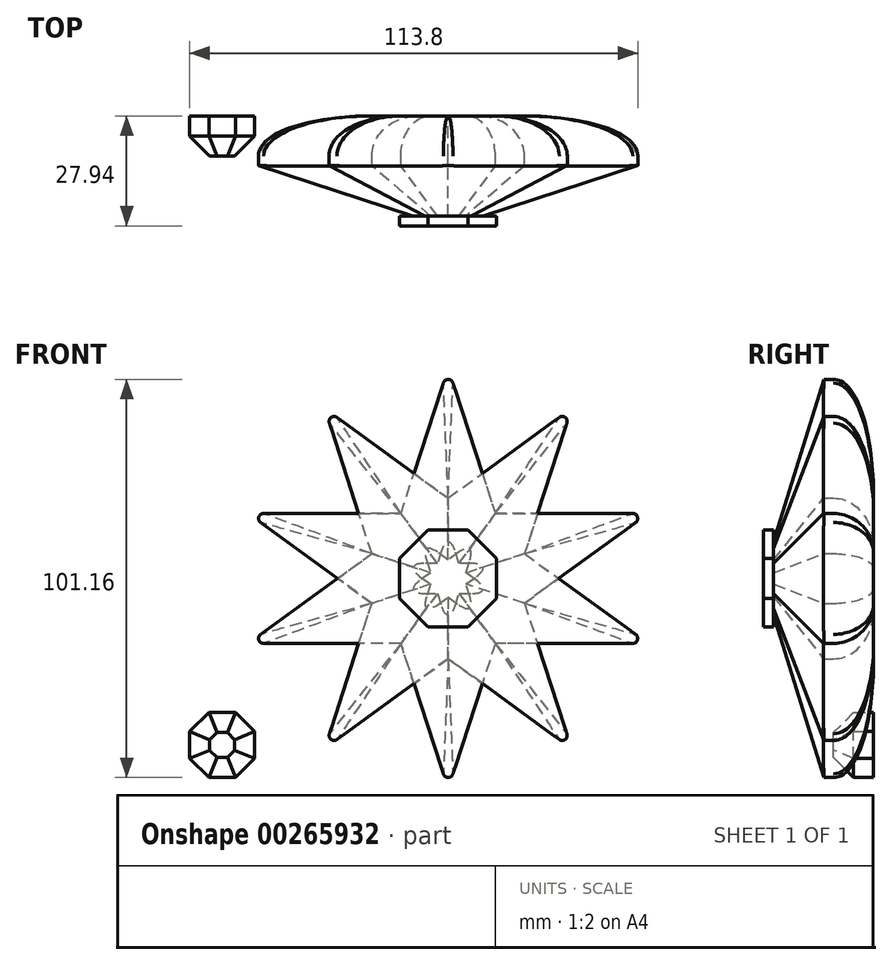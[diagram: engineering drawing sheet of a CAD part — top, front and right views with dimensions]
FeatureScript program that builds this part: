
annotation { "Feature Type Name" : "Feature", "Feature Type Description" : "" }
export const myFeature = defineFeature(function(context is Context, id is Id, definition is map)
    precondition{}
    {
        {
            var Q0;
            Q0=qCreatedBy(makeId("Front.planeOp"),FACE);
            var sketch = newSketch(context, id + "F0", { "sketchPlane" : qUnion([Q0])});
            skPoint(sketch, "E0.0.midPoint", {"position": v(0, 43.21) * mm});
            skLineSegment(sketch, "E1", {"start": v(50.8, -16.5) * mm, "end": v(-50.8, -16.5) * mm});
            skLineSegment(sketch, "E2", {"start": v(-50.8, -16.5) * mm, "end": v(31.4, 43.21) * mm});
            skLineSegment(sketch, "E3", {"start": v(31.4, 43.21) * mm, "end": v(0, -53.41) * mm});
            skLineSegment(sketch, "E4", {"start": v(0, -53.41) * mm, "end": v(-31.4, 43.21) * mm});
            skLineSegment(sketch, "E5", {"start": v(-31.4, 43.21) * mm, "end": v(50.8, -16.5) * mm});
            skSolve(sketch);
        }
        {
            var Q0;
            Q0=qCreatedBy(makeId("Front.planeOp"),FACE);
            var sketch = newSketch(context, id + "F1", { "sketchPlane" : qUnion([Q0])});
            skPoint(sketch, "E6.0.midPoint", {"position": v(0, -43.21) * mm});
            skLineSegment(sketch, "E7", {"start": v(-31.4, -43.21) * mm, "end": v(0, 53.41) * mm});
            skLineSegment(sketch, "E8", {"start": v(0, 53.41) * mm, "end": v(31.4, -43.21) * mm});
            skLineSegment(sketch, "E9", {"start": v(-50.8, 16.5) * mm, "end": v(31.4, -43.21) * mm});
            skLineSegment(sketch, "E10", {"start": v(50.8, 16.5) * mm, "end": v(-50.8, 16.5) * mm});
            skLineSegment(sketch, "E11", {"start": v(-31.4, -43.21) * mm, "end": v(50.8, 16.5) * mm});
            skSolve(sketch);
        }
        {
            var Q0;
            {var subQ0=sQuery(id+"F0.wireOp",EDGE,"E2");var subQ1=sQuery(id+"F0.wireOp",EDGE,"E1");var subQ2=makeQuery(id+"F0.imprint","INTERSECT",VERTEX,{"derivedFrom":[subQ1,subQ0]});Q0=makeQuery(id+"F0.imprint","IMPRINT",FACE,{"disambiguationData":[TD([[makeQuery(id+"F0.imprint","IMPRINT",EDGE,{"disambiguationData":[TD([[subQ2,1.0]])],"derivedFrom":subQ1}),-1.0]])]});}
            var Q1;
            {var subQ0=sQuery(id+"F0.wireOp",EDGE,"E4");var subQ1=sQuery(id+"F0.wireOp",EDGE,"E2");var subQ2=makeQuery(id+"F0.imprint","INTERSECT",VERTEX,{"derivedFrom":[subQ1,subQ0]});Q1=makeQuery(id+"F0.imprint","IMPRINT",FACE,{"disambiguationData":[TD([[makeQuery(id+"F0.imprint","IMPRINT",EDGE,{"disambiguationData":[TD([[subQ2,-1.0]])],"derivedFrom":subQ1}),1.0]])]});}
            var Q2;
            {var subQ1=sQuery(id+"F0.wireOp",EDGE,"E1");var subQ5=sQuery(id+"F0.wireOp",EDGE,"E3");var subQ6=makeQuery(id+"F0.imprint","INTERSECT",VERTEX,{"derivedFrom":[subQ1,subQ5]});Q2=makeQuery(id+"F0.imprint","IMPRINT",FACE,{"disambiguationData":[TD([[makeQuery(id+"F0.imprint","IMPRINT",EDGE,{"disambiguationData":[TD([[subQ6,-1.0]])],"derivedFrom":subQ1}),-1.0]])]});}
            var Q3;
            {var subQ0=sQuery(id+"F0.wireOp",EDGE,"E3");var subQ1=sQuery(id+"F0.wireOp",EDGE,"E2");var subQ2=makeQuery(id+"F0.imprint","INTERSECT",VERTEX,{"derivedFrom":[subQ1,subQ0]});Q3=makeQuery(id+"F0.imprint","IMPRINT",FACE,{"disambiguationData":[TD([[makeQuery(id+"F0.imprint","IMPRINT",EDGE,{"disambiguationData":[TD([[subQ2,1.0]])],"derivedFrom":subQ1}),-1.0]])]});}
            var Q4;
            {var subQ0=sQuery(id+"F0.wireOp",EDGE,"E5");var subQ1=sQuery(id+"F0.wireOp",EDGE,"E1");var subQ2=makeQuery(id+"F0.imprint","INTERSECT",VERTEX,{"derivedFrom":[subQ1,subQ0]});Q4=makeQuery(id+"F0.imprint","IMPRINT",FACE,{"disambiguationData":[TD([[makeQuery(id+"F0.imprint","IMPRINT",EDGE,{"disambiguationData":[TD([[subQ2,-1.0]])],"derivedFrom":subQ1}),-1.0]])]});}
            var Q5;
            {var subQ0=sQuery(id+"F0.wireOp",EDGE,"E3");var subQ1=sQuery(id+"F0.wireOp",EDGE,"E1");var subQ2=makeQuery(id+"F0.imprint","INTERSECT",VERTEX,{"derivedFrom":[subQ1,subQ0]});Q5=makeQuery(id+"F0.imprint","IMPRINT",FACE,{"disambiguationData":[TD([[makeQuery(id+"F0.imprint","IMPRINT",EDGE,{"disambiguationData":[TD([[subQ2,-1.0]])],"derivedFrom":subQ1}),1.0]])]});}
            extrude(context, id + "F2", {"entities" : qUnion([Q0, Q1, Q2, Q3, Q4, Q5]), "depth" : 25.4 * mm});
        }
        {
            var Q0;
            Q0=makeQuery(id+"F2.opExtrude","CAP_FACE",FACE,{"disambiguationData":[OSD([sQuery(id+"F0.wireOp",EDGE,"E1"),sQuery(id+"F0.wireOp",EDGE,"E2"),sQuery(id+"F0.wireOp",EDGE,"E3"),sQuery(id+"F0.wireOp",EDGE,"E4"),sQuery(id+"F0.wireOp",EDGE,"E5")])],"isStart":false});
            chamfer(context, id + "F3", {"entities" : qUnion([Q0]), "width" : 12.7 * mm, "tangentPropagation" : true});
        }
        {
            var Q0;
            {var subQ1=sQuery(id+"F1.wireOp",EDGE,"E7");var subQ7=sQuery(id+"F1.wireOp",EDGE,"E9");var subQ9=makeQuery(id+"F1.imprint","INTERSECT",VERTEX,{"derivedFrom":[subQ1,subQ7]});Q0=makeQuery(id+"F1.imprint","IMPRINT",FACE,{"disambiguationData":[TD([[makeQuery(id+"F1.imprint","IMPRINT",EDGE,{"disambiguationData":[TD([[subQ9,-1.0]])],"derivedFrom":subQ1}),-1.0]])]});}
            var Q1;
            {var subQ0=sQuery(id+"F1.wireOp",EDGE,"E10");var subQ1=sQuery(id+"F1.wireOp",EDGE,"E8");var subQ2=makeQuery(id+"F1.imprint","INTERSECT",VERTEX,{"derivedFrom":[subQ1,subQ0]});Q1=makeQuery(id+"F1.imprint","IMPRINT",FACE,{"disambiguationData":[TD([[makeQuery(id+"F1.imprint","IMPRINT",EDGE,{"disambiguationData":[TD([[subQ2,-1.0]])],"derivedFrom":subQ1}),1.0]])]});}
            var Q2;
            {var subQ0=sQuery(id+"F1.wireOp",EDGE,"E8");var subQ1=sQuery(id+"F1.wireOp",EDGE,"E7");var subQ2=makeQuery(id+"F1.imprint","INTERSECT",VERTEX,{"derivedFrom":[subQ1,subQ0]});Q2=makeQuery(id+"F1.imprint","IMPRINT",FACE,{"disambiguationData":[TD([[makeQuery(id+"F1.imprint","IMPRINT",EDGE,{"disambiguationData":[TD([[subQ2,1.0]])],"derivedFrom":subQ1}),-1.0]])]});}
            var Q3;
            {var subQ0=sQuery(id+"F1.wireOp",EDGE,"E9");var subQ1=sQuery(id+"F1.wireOp",EDGE,"E7");var subQ2=makeQuery(id+"F1.imprint","INTERSECT",VERTEX,{"derivedFrom":[subQ1,subQ0]});Q3=makeQuery(id+"F1.imprint","IMPRINT",FACE,{"disambiguationData":[TD([[makeQuery(id+"F1.imprint","IMPRINT",EDGE,{"disambiguationData":[TD([[subQ2,-1.0]])],"derivedFrom":subQ1}),1.0]])]});}
            var Q4;
            {var subQ0=sQuery(id+"F1.wireOp",EDGE,"E11");var subQ1=sQuery(id+"F1.wireOp",EDGE,"E7");var subQ2=makeQuery(id+"F1.imprint","INTERSECT",VERTEX,{"derivedFrom":[subQ1,subQ0]});Q4=makeQuery(id+"F1.imprint","IMPRINT",FACE,{"disambiguationData":[TD([[makeQuery(id+"F1.imprint","IMPRINT",EDGE,{"disambiguationData":[TD([[subQ2,-1.0]])],"derivedFrom":subQ1}),-1.0]])]});}
            var Q5;
            {var subQ0=sQuery(id+"F1.wireOp",EDGE,"E9");var subQ1=sQuery(id+"F1.wireOp",EDGE,"E8");var subQ2=makeQuery(id+"F1.imprint","INTERSECT",VERTEX,{"derivedFrom":[subQ1,subQ0]});Q5=makeQuery(id+"F1.imprint","IMPRINT",FACE,{"disambiguationData":[TD([[makeQuery(id+"F1.imprint","IMPRINT",EDGE,{"disambiguationData":[TD([[subQ2,1.0]])],"derivedFrom":subQ1}),-1.0]])]});}
            extrude(context, id + "F4", {"entities" : qUnion([Q0, Q1, Q2, Q3, Q4, Q5]), "depth" : 25.4 * mm});
        }
        {
            var Q0;
            Q0=makeQuery(id+"F4.opExtrude","CAP_FACE",FACE,{"disambiguationData":[OSD([sQuery(id+"F1.wireOp",EDGE,"E7"),sQuery(id+"F1.wireOp",EDGE,"E8"),sQuery(id+"F1.wireOp",EDGE,"E9"),sQuery(id+"F1.wireOp",EDGE,"E10"),sQuery(id+"F1.wireOp",EDGE,"E11")])],"isStart":false});
            chamfer(context, id + "F5", {"entities" : qUnion([Q0]), "width" : 12.7 * mm, "tangentPropagation" : true});
        }
        {
            var Q0;
            Q0=makeQuery(id+"F4.opExtrude","CAP_FACE",FACE,{"disambiguationData":[OSD([sQuery(id+"F1.wireOp",EDGE,"E7"),sQuery(id+"F1.wireOp",EDGE,"E8"),sQuery(id+"F1.wireOp",EDGE,"E9"),sQuery(id+"F1.wireOp",EDGE,"E10"),sQuery(id+"F1.wireOp",EDGE,"E11")])],"isStart":false});
            var sketch = newSketch(context, id + "F6", { "sketchPlane" : qUnion([Q0])});
            skCircle(sketch, "E12.cCircle", {"center": v(0, 0) * mm, "radius": 12.32 * mm, "construction": true});
            skLineSegment(sketch, "E12.0", {"start": v(-5.1, 12.32) * mm, "end": v(5.1, 12.32) * mm});
            skLineSegment(sketch, "E12.1", {"start": v(5.1, 12.32) * mm, "end": v(12.32, 5.1) * mm});
            skLineSegment(sketch, "E12.2", {"start": v(12.32, 5.1) * mm, "end": v(12.32, -5.1) * mm});
            skLineSegment(sketch, "E12.3", {"start": v(12.32, -5.1) * mm, "end": v(5.1, -12.32) * mm});
            skLineSegment(sketch, "E12.4", {"start": v(5.1, -12.32) * mm, "end": v(-5.1, -12.32) * mm});
            skLineSegment(sketch, "E12.5", {"start": v(-5.1, -12.32) * mm, "end": v(-12.32, -5.1) * mm});
            skLineSegment(sketch, "E12.6", {"start": v(-12.32, -5.1) * mm, "end": v(-12.32, 5.1) * mm});
            skLineSegment(sketch, "E12.7", {"start": v(-12.32, 5.1) * mm, "end": v(-5.1, 12.32) * mm});
            skPoint(sketch, "E12.0.midPoint", {"position": v(0, 12.32) * mm});
            skSolve(sketch);
        }
        {
            var Q0;
            {var subQ17=sQuery(id+"F6.wireOp",EDGE,"E12.1");Q0=makeQuery(id+"F6.imprint","IMPRINT",FACE,{"disambiguationData":[TD([[makeQuery(id+"F6.imprint","IMPRINT",EDGE,{"derivedFrom":subQ17}),-1.0]])]});}
            var Q1;
            {var subQ0=sQuery(id+"F1.wireOp",EDGE,"E11");var subQ1=sQuery(id+"F1.wireOp",EDGE,"E10");var subQ2=sQuery(id+"F1.wireOp",EDGE,"E9");var subQ3=sQuery(id+"F1.wireOp",EDGE,"E8");var subQ4=sQuery(id+"F1.wireOp",EDGE,"E7");var subQ5=makeQuery(id+"F4.opExtrude","CAP_FACE",FACE,{"disambiguationData":[OSD([subQ4,subQ3,subQ2,subQ1,subQ0])],"isStart":false});var subQ8=makeQuery(id+"F1.imprint","INTERSECT",VERTEX,{"derivedFrom":[subQ4,subQ0]});Q1=makeQuery(id+"F6.imprint","IMPRINT",FACE,{"disambiguationData":[TD([[makeQuery(id+"F6.imprint","IMPRINT",EDGE,{"derivedFrom":makeQuery(id+"F5.opChamfer","BLEND_EDGE",EDGE,{"blendedFrom":[makeQuery(id+"F4.opExtrude","CAP_EDGE",EDGE,{"disambiguationData":[OSD([subQ4]),TDD([makeQuery(id+"F1.imprint","IMPRINT",EDGE,{"disambiguationData":[TD([[subQ8,-1.0]])],"derivedFrom":subQ4})])],"isStart":false}),subQ5],"blendedInto":[subQ5]})}),1.0]])]});}
            extrude(context, id + "F7", {"entities" : qUnion([Q0, Q1]), "depth" : 2.54 * mm});
        }
        {
            var Q0;
            Q0=makeQuery(id+"F2.opExtrude","SWEPT_EDGE",EDGE,{"disambiguationData":[OSD([sQuery(id+"F0.wireOp",EDGE,"E2"),sQuery(id+"F0.wireOp",EDGE,"E3")])]});
            var Q1;
            Q1=makeQuery(id+"F4.opExtrude","SWEPT_EDGE",EDGE,{"disambiguationData":[OSD([sQuery(id+"F1.wireOp",EDGE,"E10"),sQuery(id+"F1.wireOp",EDGE,"E11")])]});
            var Q2;
            Q2=makeQuery(id+"F2.opExtrude","SWEPT_EDGE",EDGE,{"disambiguationData":[OSD([sQuery(id+"F0.wireOp",EDGE,"E1"),sQuery(id+"F0.wireOp",EDGE,"E5")])]});
            var Q3;
            Q3=makeQuery(id+"F4.opExtrude","SWEPT_EDGE",EDGE,{"disambiguationData":[OSD([sQuery(id+"F1.wireOp",EDGE,"E8"),sQuery(id+"F1.wireOp",EDGE,"E9")])]});
            var Q4;
            Q4=makeQuery(id+"F2.opExtrude","SWEPT_EDGE",EDGE,{"disambiguationData":[OSD([sQuery(id+"F0.wireOp",EDGE,"E3"),sQuery(id+"F0.wireOp",EDGE,"E4")])]});
            var Q5;
            Q5=makeQuery(id+"F4.opExtrude","SWEPT_EDGE",EDGE,{"disambiguationData":[OSD([sQuery(id+"F1.wireOp",EDGE,"E7"),sQuery(id+"F1.wireOp",EDGE,"E11")])]});
            var Q6;
            Q6=makeQuery(id+"F2.opExtrude","SWEPT_EDGE",EDGE,{"disambiguationData":[OSD([sQuery(id+"F0.wireOp",EDGE,"E1"),sQuery(id+"F0.wireOp",EDGE,"E2")])]});
            var Q7;
            Q7=makeQuery(id+"F4.opExtrude","SWEPT_EDGE",EDGE,{"disambiguationData":[OSD([sQuery(id+"F1.wireOp",EDGE,"E9"),sQuery(id+"F1.wireOp",EDGE,"E10")])]});
            var Q8;
            Q8=makeQuery(id+"F2.opExtrude","SWEPT_EDGE",EDGE,{"disambiguationData":[OSD([sQuery(id+"F0.wireOp",EDGE,"E4"),sQuery(id+"F0.wireOp",EDGE,"E5")])]});
            var Q9;
            Q9=makeQuery(id+"F4.opExtrude","SWEPT_EDGE",EDGE,{"disambiguationData":[OSD([sQuery(id+"F1.wireOp",EDGE,"E7"),sQuery(id+"F1.wireOp",EDGE,"E8")])]});
            fillet(context, id + "F8", {"entities" : qUnion([Q0, Q1, Q2, Q3, Q4, Q5, Q6, Q7, Q8, Q9]), "radius" : 1.27 * mm, "tangentPropagation" : true, "allowEdgeOverflow" : false});
        }
        {
            var Q0;
            {var subQ0=sQuery(id+"F0.wireOp",EDGE,"E4");var subQ1=sQuery(id+"F0.wireOp",EDGE,"E3");var subQ2=makeQuery(id+"F0.imprint","INTERSECT",VERTEX,{"derivedFrom":[subQ1,subQ0]});Q0=makeQuery(id+"F3.opChamfer","BLEND_EDGE",EDGE,{"blendedFrom":[makeQuery(id+"F2.opExtrude","CAP_EDGE",EDGE,{"disambiguationData":[OSD([subQ1]),TDD([makeQuery(id+"F0.imprint","IMPRINT",EDGE,{"disambiguationData":[TD([[subQ2,1.0]])],"derivedFrom":subQ1})])],"isStart":false}),makeQuery(id+"F2.opExtrude","CAP_EDGE",EDGE,{"disambiguationData":[OSD([subQ0]),TDD([makeQuery(id+"F0.imprint","IMPRINT",EDGE,{"disambiguationData":[TD([[subQ2,-1.0]])],"derivedFrom":subQ0})])],"isStart":false})],"blendedInto":[]});}
            var Q1;
            {var subQ0=sQuery(id+"F1.wireOp",EDGE,"E9");var subQ1=sQuery(id+"F1.wireOp",EDGE,"E8");var subQ2=makeQuery(id+"F1.imprint","INTERSECT",VERTEX,{"derivedFrom":[subQ1,subQ0]});Q1=makeQuery(id+"F5.opChamfer","BLEND_EDGE",EDGE,{"blendedFrom":[makeQuery(id+"F4.opExtrude","CAP_EDGE",EDGE,{"disambiguationData":[OSD([subQ1]),TDD([makeQuery(id+"F1.imprint","IMPRINT",EDGE,{"disambiguationData":[TD([[subQ2,1.0]])],"derivedFrom":subQ1})])],"isStart":false}),makeQuery(id+"F4.opExtrude","CAP_EDGE",EDGE,{"disambiguationData":[OSD([subQ0]),TDD([makeQuery(id+"F1.imprint","IMPRINT",EDGE,{"disambiguationData":[TD([[subQ2,1.0]])],"derivedFrom":subQ0})])],"isStart":false})],"blendedInto":[]});}
            var Q2;
            {var subQ0=sQuery(id+"F0.wireOp",EDGE,"E5");var subQ1=sQuery(id+"F0.wireOp",EDGE,"E1");var subQ2=makeQuery(id+"F0.imprint","INTERSECT",VERTEX,{"derivedFrom":[subQ1,subQ0]});Q2=makeQuery(id+"F3.opChamfer","BLEND_EDGE",EDGE,{"blendedFrom":[makeQuery(id+"F2.opExtrude","CAP_EDGE",EDGE,{"disambiguationData":[OSD([subQ1]),TDD([makeQuery(id+"F0.imprint","IMPRINT",EDGE,{"disambiguationData":[TD([[subQ2,-1.0]])],"derivedFrom":subQ1})])],"isStart":false}),makeQuery(id+"F2.opExtrude","CAP_EDGE",EDGE,{"disambiguationData":[OSD([subQ0]),TDD([makeQuery(id+"F0.imprint","IMPRINT",EDGE,{"disambiguationData":[TD([[subQ2,1.0]])],"derivedFrom":subQ0})])],"isStart":false})],"blendedInto":[]});}
            var Q3;
            {var subQ0=sQuery(id+"F1.wireOp",EDGE,"E11");var subQ1=sQuery(id+"F1.wireOp",EDGE,"E10");var subQ2=makeQuery(id+"F1.imprint","INTERSECT",VERTEX,{"derivedFrom":[subQ1,subQ0]});Q3=makeQuery(id+"F5.opChamfer","BLEND_EDGE",EDGE,{"blendedFrom":[makeQuery(id+"F4.opExtrude","CAP_EDGE",EDGE,{"disambiguationData":[OSD([subQ1]),TDD([makeQuery(id+"F1.imprint","IMPRINT",EDGE,{"disambiguationData":[TD([[subQ2,-1.0]])],"derivedFrom":subQ1})])],"isStart":false}),makeQuery(id+"F4.opExtrude","CAP_EDGE",EDGE,{"disambiguationData":[OSD([subQ0]),TDD([makeQuery(id+"F1.imprint","IMPRINT",EDGE,{"disambiguationData":[TD([[subQ2,1.0]])],"derivedFrom":subQ0})])],"isStart":false})],"blendedInto":[]});}
            var Q4;
            {var subQ0=sQuery(id+"F0.wireOp",EDGE,"E3");var subQ1=sQuery(id+"F0.wireOp",EDGE,"E2");var subQ2=makeQuery(id+"F0.imprint","INTERSECT",VERTEX,{"derivedFrom":[subQ1,subQ0]});Q4=makeQuery(id+"F3.opChamfer","BLEND_EDGE",EDGE,{"blendedFrom":[makeQuery(id+"F2.opExtrude","CAP_EDGE",EDGE,{"disambiguationData":[OSD([subQ1]),TDD([makeQuery(id+"F0.imprint","IMPRINT",EDGE,{"disambiguationData":[TD([[subQ2,1.0]])],"derivedFrom":subQ1})])],"isStart":false}),makeQuery(id+"F2.opExtrude","CAP_EDGE",EDGE,{"disambiguationData":[OSD([subQ0]),TDD([makeQuery(id+"F0.imprint","IMPRINT",EDGE,{"disambiguationData":[TD([[subQ2,-1.0]])],"derivedFrom":subQ0})])],"isStart":false})],"blendedInto":[]});}
            var Q5;
            {var subQ0=sQuery(id+"F1.wireOp",EDGE,"E8");var subQ1=sQuery(id+"F1.wireOp",EDGE,"E7");var subQ2=makeQuery(id+"F1.imprint","INTERSECT",VERTEX,{"derivedFrom":[subQ1,subQ0]});Q5=makeQuery(id+"F5.opChamfer","BLEND_EDGE",EDGE,{"blendedFrom":[makeQuery(id+"F4.opExtrude","CAP_EDGE",EDGE,{"disambiguationData":[OSD([subQ1]),TDD([makeQuery(id+"F1.imprint","IMPRINT",EDGE,{"disambiguationData":[TD([[subQ2,1.0]])],"derivedFrom":subQ1})])],"isStart":false}),makeQuery(id+"F4.opExtrude","CAP_EDGE",EDGE,{"disambiguationData":[OSD([subQ0]),TDD([makeQuery(id+"F1.imprint","IMPRINT",EDGE,{"disambiguationData":[TD([[subQ2,-1.0]])],"derivedFrom":subQ0})])],"isStart":false})],"blendedInto":[]});}
            var Q6;
            {var subQ0=sQuery(id+"F0.wireOp",EDGE,"E5");var subQ1=sQuery(id+"F0.wireOp",EDGE,"E4");var subQ2=makeQuery(id+"F0.imprint","INTERSECT",VERTEX,{"derivedFrom":[subQ1,subQ0]});Q6=makeQuery(id+"F3.opChamfer","BLEND_EDGE",EDGE,{"blendedFrom":[makeQuery(id+"F2.opExtrude","CAP_EDGE",EDGE,{"disambiguationData":[OSD([subQ1]),TDD([makeQuery(id+"F0.imprint","IMPRINT",EDGE,{"disambiguationData":[TD([[subQ2,1.0]])],"derivedFrom":subQ1})])],"isStart":false}),makeQuery(id+"F2.opExtrude","CAP_EDGE",EDGE,{"disambiguationData":[OSD([subQ0]),TDD([makeQuery(id+"F0.imprint","IMPRINT",EDGE,{"disambiguationData":[TD([[subQ2,-1.0]])],"derivedFrom":subQ0})])],"isStart":false})],"blendedInto":[]});}
            var Q7;
            {var subQ0=sQuery(id+"F1.wireOp",EDGE,"E10");var subQ1=sQuery(id+"F1.wireOp",EDGE,"E9");var subQ2=makeQuery(id+"F1.imprint","INTERSECT",VERTEX,{"derivedFrom":[subQ1,subQ0]});Q7=makeQuery(id+"F5.opChamfer","BLEND_EDGE",EDGE,{"blendedFrom":[makeQuery(id+"F4.opExtrude","CAP_EDGE",EDGE,{"disambiguationData":[OSD([subQ1]),TDD([makeQuery(id+"F1.imprint","IMPRINT",EDGE,{"disambiguationData":[TD([[subQ2,-1.0]])],"derivedFrom":subQ1})])],"isStart":false}),makeQuery(id+"F4.opExtrude","CAP_EDGE",EDGE,{"disambiguationData":[OSD([subQ0]),TDD([makeQuery(id+"F1.imprint","IMPRINT",EDGE,{"disambiguationData":[TD([[subQ2,1.0]])],"derivedFrom":subQ0})])],"isStart":false})],"blendedInto":[]});}
            var Q8;
            {var subQ0=sQuery(id+"F0.wireOp",EDGE,"E2");var subQ1=sQuery(id+"F0.wireOp",EDGE,"E1");var subQ2=makeQuery(id+"F0.imprint","INTERSECT",VERTEX,{"derivedFrom":[subQ1,subQ0]});Q8=makeQuery(id+"F3.opChamfer","BLEND_EDGE",EDGE,{"blendedFrom":[makeQuery(id+"F2.opExtrude","CAP_EDGE",EDGE,{"disambiguationData":[OSD([subQ1]),TDD([makeQuery(id+"F0.imprint","IMPRINT",EDGE,{"disambiguationData":[TD([[subQ2,1.0]])],"derivedFrom":subQ1})])],"isStart":false}),makeQuery(id+"F2.opExtrude","CAP_EDGE",EDGE,{"disambiguationData":[OSD([subQ0]),TDD([makeQuery(id+"F0.imprint","IMPRINT",EDGE,{"disambiguationData":[TD([[subQ2,-1.0]])],"derivedFrom":subQ0})])],"isStart":false})],"blendedInto":[]});}
            var Q9;
            {var subQ0=sQuery(id+"F1.wireOp",EDGE,"E11");var subQ1=sQuery(id+"F1.wireOp",EDGE,"E7");var subQ2=makeQuery(id+"F1.imprint","INTERSECT",VERTEX,{"derivedFrom":[subQ1,subQ0]});Q9=makeQuery(id+"F5.opChamfer","BLEND_EDGE",EDGE,{"blendedFrom":[makeQuery(id+"F4.opExtrude","CAP_EDGE",EDGE,{"disambiguationData":[OSD([subQ1]),TDD([makeQuery(id+"F1.imprint","IMPRINT",EDGE,{"disambiguationData":[TD([[subQ2,-1.0]])],"derivedFrom":subQ1})])],"isStart":false}),makeQuery(id+"F4.opExtrude","CAP_EDGE",EDGE,{"disambiguationData":[OSD([subQ0]),TDD([makeQuery(id+"F1.imprint","IMPRINT",EDGE,{"disambiguationData":[TD([[subQ2,-1.0]])],"derivedFrom":subQ0})])],"isStart":false})],"blendedInto":[]});}
            fillet(context, id + "F9", {"entities" : qUnion([Q0, Q1, Q2, Q3, Q4, Q5, Q6, Q7, Q8, Q9]), "radius" : 2.54 * mm, "tangentPropagation" : true, "allowEdgeOverflow" : false});
        }
        {
            var Q0;
            Q0=makeQuery(id+"F4.opExtrude","CAP_FACE",FACE,{"disambiguationData":[OSD([sQuery(id+"F1.wireOp",EDGE,"E7"),sQuery(id+"F1.wireOp",EDGE,"E8"),sQuery(id+"F1.wireOp",EDGE,"E9"),sQuery(id+"F1.wireOp",EDGE,"E10"),sQuery(id+"F1.wireOp",EDGE,"E11")])],"isStart":true});
            var Q1;
            Q1=makeQuery(id+"F2.opExtrude","CAP_FACE",FACE,{"disambiguationData":[OSD([sQuery(id+"F0.wireOp",EDGE,"E1"),sQuery(id+"F0.wireOp",EDGE,"E2"),sQuery(id+"F0.wireOp",EDGE,"E3"),sQuery(id+"F0.wireOp",EDGE,"E4"),sQuery(id+"F0.wireOp",EDGE,"E5")])],"isStart":true});
            fillet(context, id + "F10", {"entities" : qUnion([Q0, Q1]), "radius" : 10.16 * mm, "tangentPropagation" : true, "allowEdgeOverflow" : false});
        }
        {
            var Q0;
            Q0=qCreatedBy(makeId("Front.planeOp"),FACE);
            var sketch = newSketch(context, id + "F11", { "sketchPlane" : qUnion([Q0])});
            skCircle(sketch, "E13.cCircle", {"center": v(-57.38, -42.33) * mm, "radius": 8.26 * mm, "construction": true});
            skLineSegment(sketch, "E13.0", {"start": v(-60.8, -34.08) * mm, "end": v(-53.96, -34.08) * mm});
            skLineSegment(sketch, "E13.1", {"start": v(-53.96, -34.08) * mm, "end": v(-49.13, -38.92) * mm});
            skLineSegment(sketch, "E13.2", {"start": v(-49.13, -38.92) * mm, "end": v(-49.13, -45.75) * mm});
            skLineSegment(sketch, "E13.3", {"start": v(-49.13, -45.75) * mm, "end": v(-53.96, -50.59) * mm});
            skLineSegment(sketch, "E13.4", {"start": v(-53.96, -50.59) * mm, "end": v(-60.8, -50.59) * mm});
            skLineSegment(sketch, "E13.5", {"start": v(-60.8, -50.59) * mm, "end": v(-65.64, -45.75) * mm});
            skLineSegment(sketch, "E13.6", {"start": v(-65.64, -45.75) * mm, "end": v(-65.64, -38.92) * mm});
            skLineSegment(sketch, "E13.7", {"start": v(-65.64, -38.92) * mm, "end": v(-60.8, -34.08) * mm});
            skPoint(sketch, "E13.0.midPoint", {"position": v(-57.38, -34.08) * mm});
            skSolve(sketch);
        }
        {
            var Q0;
            Q0=makeQuery(id+"F11.imprint","IMPRINT",FACE,{"disambiguationData":[TD([[makeQuery(id+"F11.imprint","IMPRINT",EDGE,{"derivedFrom":sQuery(id+"F11.wireOp",EDGE,"E13.0")}),-1.0]])]});
            extrude(context, id + "F12", {"entities" : qUnion([Q0]), "depth" : 10.16 * mm});
        }
        {
            var Q0;
            Q0=makeQuery(id+"F12.opExtrude","CAP_EDGE",EDGE,{"disambiguationData":[OSD([sQuery(id+"F11.wireOp",EDGE,"E13.5")])],"isStart":false});
            var Q1;
            Q1=makeQuery(id+"F12.opExtrude","CAP_FACE",FACE,{"disambiguationData":[OSD([sQuery(id+"F11.wireOp",EDGE,"E13.0"),sQuery(id+"F11.wireOp",EDGE,"E13.1"),sQuery(id+"F11.wireOp",EDGE,"E13.2"),sQuery(id+"F11.wireOp",EDGE,"E13.3"),sQuery(id+"F11.wireOp",EDGE,"E13.4"),sQuery(id+"F11.wireOp",EDGE,"E13.5"),sQuery(id+"F11.wireOp",EDGE,"E13.6"),sQuery(id+"F11.wireOp",EDGE,"E13.7")])],"isStart":false});
            chamfer(context, id + "F13", {"entities" : qUnion([Q0, Q1]), "width" : 5.08 * mm, "tangentPropagation" : true});
        }
    });
